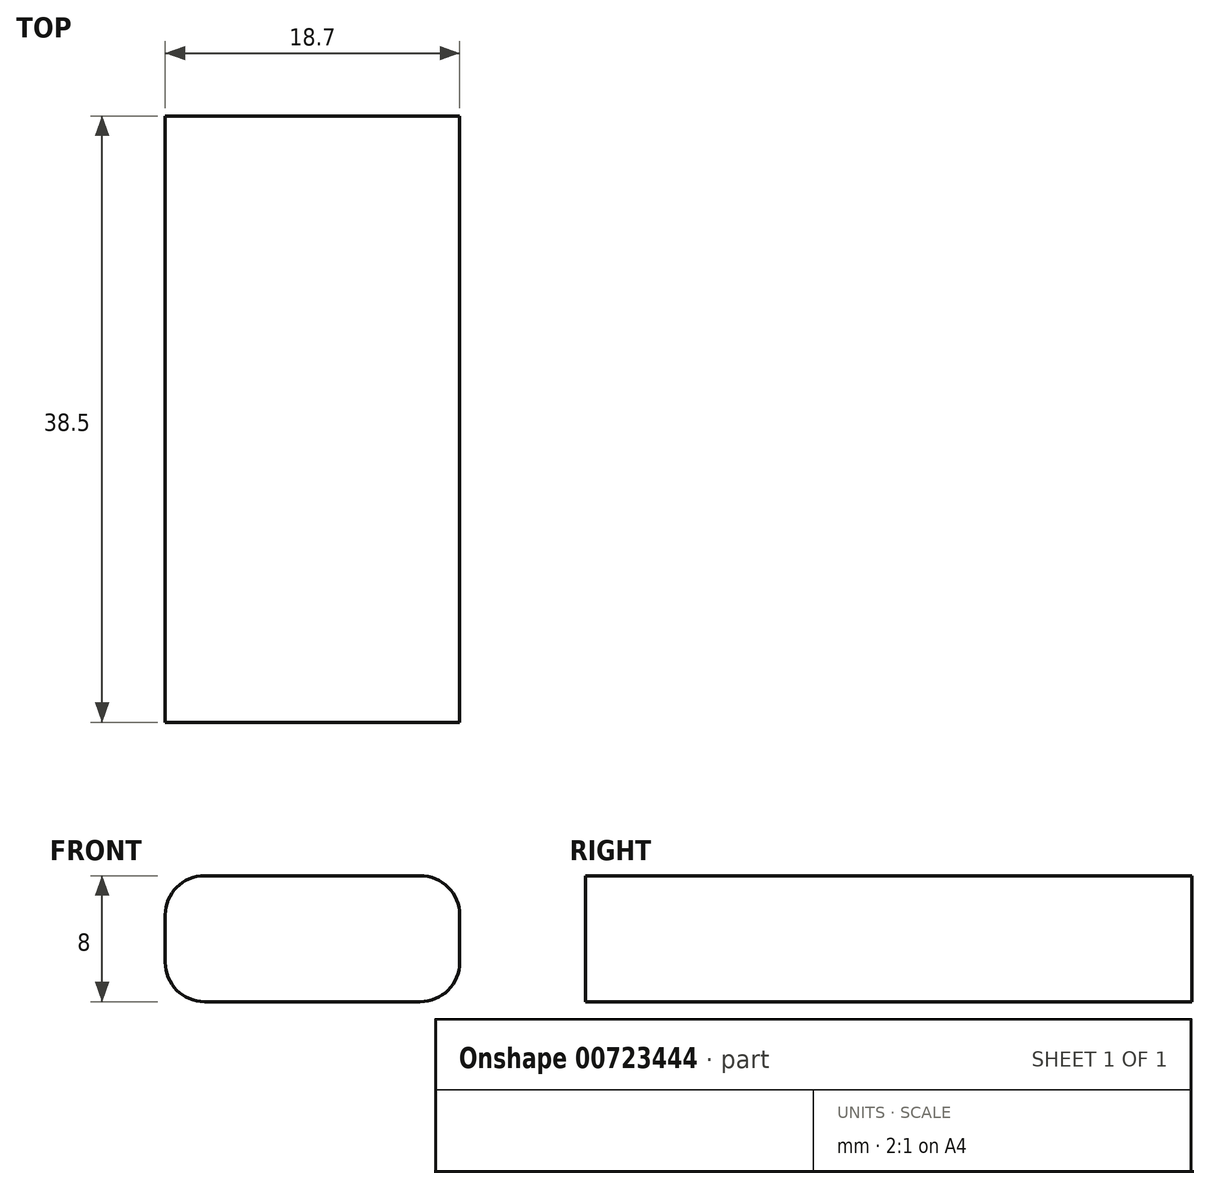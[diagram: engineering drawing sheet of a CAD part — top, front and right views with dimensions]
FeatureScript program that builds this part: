
annotation { "Feature Type Name" : "Feature", "Feature Type Description" : "" }
export const myFeature = defineFeature(function(context is Context, id is Id, definition is map)
    precondition{}
    {
        {
            var Q0;
            Q0=qCreatedBy(makeId("Top.planeOp"),FACE);
            var sketch = newSketch(context, id + "F0", { "sketchPlane" : qUnion([Q0])});
            skLineSegment(sketch, "E0.bottom", {"start": v(9.35, 19.25) * mm, "end": v(-9.35, 19.25) * mm});
            skLineSegment(sketch, "E0.top", {"start": v(9.35, -19.25) * mm, "end": v(-9.35, -19.25) * mm});
            skLineSegment(sketch, "E0.left", {"start": v(9.35, 19.25) * mm, "end": v(9.35, -19.25) * mm});
            skLineSegment(sketch, "E0.right", {"start": v(-9.35, 19.25) * mm, "end": v(-9.35, -19.25) * mm});
            skPoint(sketch, "E0.middle", {"position": v(0, 0) * mm});
            skSolve(sketch);
        }
        {
            var Q0;
            Q0=qSketchRegion(id+"F0",true);
            extrude(context, id + "F1", {"entities" : qUnion([Q0]), "depth" : 8 * mm, "offsetDistance" : 25 * mm});
        }
        {
            var Q0;
            Q0=makeQuery(id+"F1.opExtrude","CAP_EDGE",EDGE,{"disambiguationData":[OSD([sQuery(id+"F0.wireOp",EDGE,"E0.left")])],"isStart":false});
            var Q1;
            Q1=makeQuery(id+"F1.opExtrude","CAP_EDGE",EDGE,{"disambiguationData":[OSD([sQuery(id+"F0.wireOp",EDGE,"E0.left")])],"isStart":true});
            var Q2;
            Q2=makeQuery(id+"F1.opExtrude","CAP_EDGE",EDGE,{"disambiguationData":[OSD([sQuery(id+"F0.wireOp",EDGE,"E0.right")])],"isStart":false});
            var Q3;
            Q3=makeQuery(id+"F1.opExtrude","CAP_EDGE",EDGE,{"disambiguationData":[OSD([sQuery(id+"F0.wireOp",EDGE,"E0.right")])],"isStart":true});
            fillet(context, id + "F2", {"entities" : qUnion([Q0, Q1, Q2, Q3]), "radius" : 2.5 * mm, "tangentPropagation" : true, "allowEdgeOverflow" : false});
        }
    });
